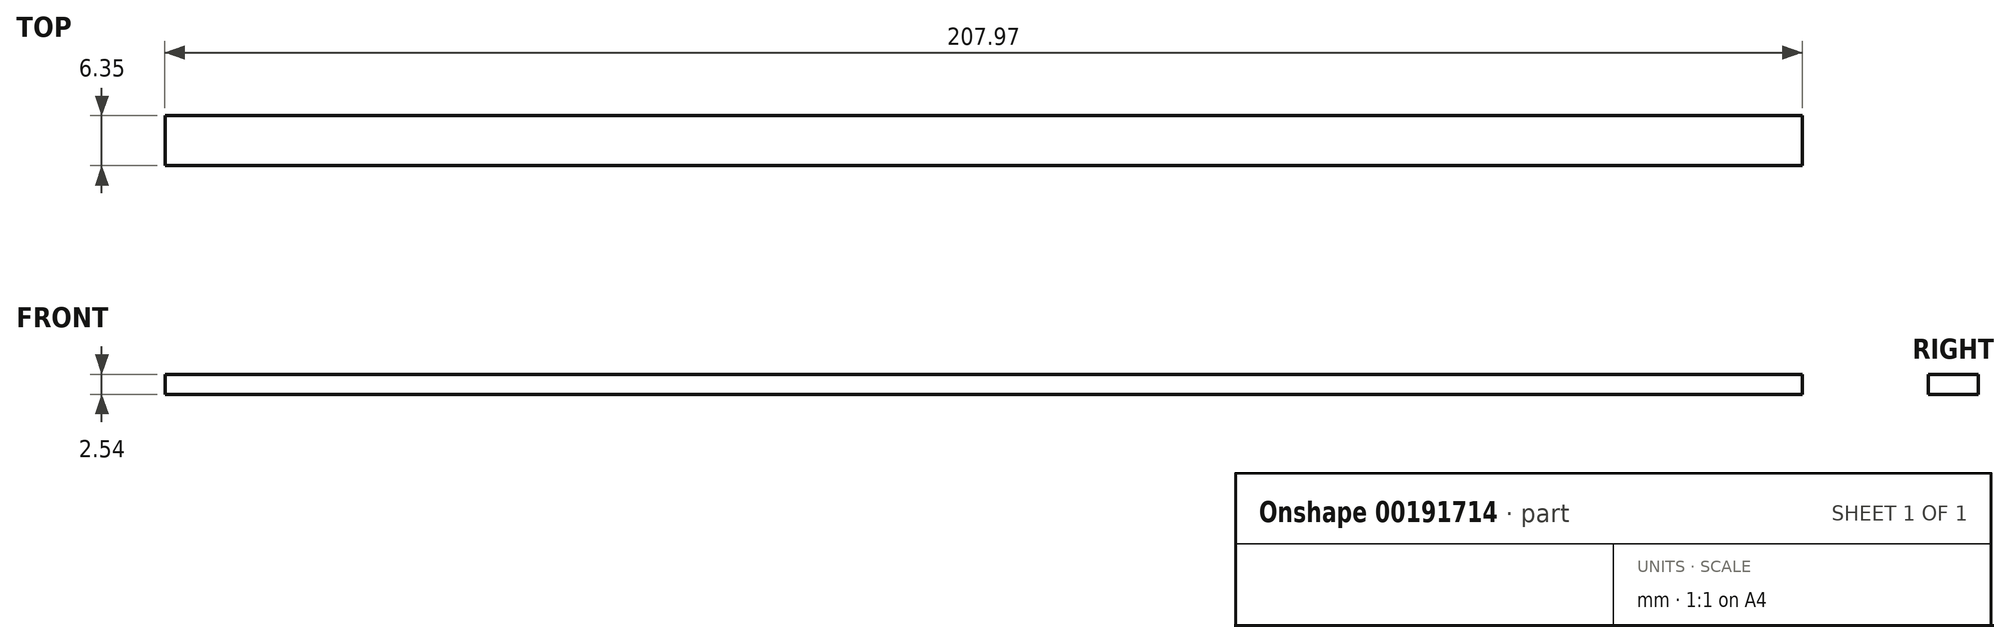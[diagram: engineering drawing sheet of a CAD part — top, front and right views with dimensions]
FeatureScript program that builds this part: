
annotation { "Feature Type Name" : "Feature", "Feature Type Description" : "" }
export const myFeature = defineFeature(function(context is Context, id is Id, definition is map)
    precondition{}
    {
        {
            var Q0;
            Q0=qCreatedBy(makeId("Top.planeOp"),FACE);
            var sketch = newSketch(context, id + "F0", { "sketchPlane" : qUnion([Q0])});
            skLineSegment(sketch, "E0.bottom", {"start": v(-81.7, 0.83) * mm, "end": v(126.26, 0.83) * mm});
            skLineSegment(sketch, "E0.top", {"start": v(-81.7, -5.52) * mm, "end": v(126.26, -5.52) * mm});
            skLineSegment(sketch, "E0.left", {"start": v(-81.7, 0.83) * mm, "end": v(-81.7, -5.52) * mm});
            skLineSegment(sketch, "E0.right", {"start": v(126.26, 0.83) * mm, "end": v(126.26, -5.52) * mm});
            skSolve(sketch);
        }
        {
            var Q0;
            Q0=makeQuery(id+"F0.imprint","IMPRINT",FACE,{"disambiguationData":[TD([[makeQuery(id+"F0.imprint","IMPRINT",EDGE,{"derivedFrom":sQuery(id+"F0.wireOp",EDGE,"E0.bottom")}),-1.0]])]});
            extrude(context, id + "F1", {"entities" : qUnion([Q0]), "depth" : 2.54 * mm});
        }
    });
